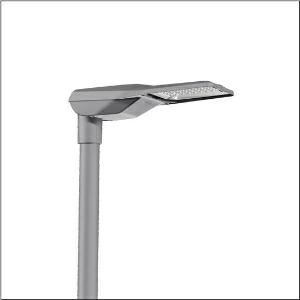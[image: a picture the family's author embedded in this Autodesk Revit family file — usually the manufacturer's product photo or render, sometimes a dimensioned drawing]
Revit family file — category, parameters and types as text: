
# Revit family: streetlight_sl_21_iq_mini___st0_8a_5xe2c41g08hb_fab9
name_source: partatom
category: Lighting Fixtures
units: mm (PartAtom-declared; Revit-internal decimal feet)

## family parameters
Cut with Voids When Loaded = No
Host = Face
Light Source = No
Part Type = Normal
Room Calculation Point = No
Round Connector Dimension = Use Diameter
Shared = No

## types (1)
- --- (1 x LED, 9860 lm, 70.9 W, 4000K)
    Apparent Load = 71 VA
    CIE Flux Codes = 38 75 97 100 100
    Color Rendering = 70
    Color Temperature = 4000K
    Default Elevation = 1800 mm
    Description = Streetlight SL 21 iQ mini, mast luminaire, primary light control with lens, of PMMA, primary optical cover: cover, of toughened safety glass, transparent, light distribution: ST0.8a, light emission: direct distribution, primary light characteristic: asymmetric, installation type: post-top, side-entry, LED, High Power LED, rated luminous flux: 9.860lm, luminous efficacy: 139lm/W, light colour: 740, colour temperature: 4000K, control: Street-Remote, Auto-Match, Temp-Guard, Lumen-Switch, Night-Set, Smart-Wire, Light-Fading, Desk-Remote (wireless, voltage-free reading and setting of iQ features in the workshop via application-optimized NFC function/RFID function), optimised constant luminous flux control (CLO 2.0), presetting dimming linear, mains connection: 220..240V, AC, 50/60Hz, start of lifetime: 71W, end of service life: 75W, reduction: 31W, luminaire housing, of diecast aluminium, powder-coated, Siteco® metallic grey (DB 702S), corrosivity category C5 mid according to DIN EN ISO 12944, please order mast flange separately, inclination adjustable: 0°, 5°, 10°, 15°, sealing non-destructively replaceable, multi-level sealing system, length: 628mm, width: 235mm, height: 110mm, mast flange for spigot size: 42mm (side-entry): 5XC10008XM4, 60/48mm (side-entry/post-top): 5XC10108XM2, 76/60mm (side-entry/post-top): 5XC10108XM1, protection rating (complete): IP66, insulation class (complete): insulation class II (safety insulation), certification: CE, ENEC, ENEC+, VDE, impact resistance: IK09, permissible operating ambient temperature for outdoor applications: -40..+50°C, standard-compliant lighting for roads and squares, packaging unit: 1 piece

Light Distribution: ST0.8a
    Height = 110 mm
    Lamp = 1 x LED
    Lamp Light Flux = 9860 lm
    Lamp Power = 70.9 W
    Lamp count = 1
    Length = 625 mm
    Luminous efficacy = 139 lm/W
    Manufacturer = Siteco
    ModVariant = No
    Model = 5XE2C41G08HB
    Number of Poles = 1
    OnlyDefault = Yes
    Power Factor = 1
    Product Name = Streetlight SL 21 iQ mini | ST0.8a
    Product group = mast luminaire | pylon top
    ProductGroupID = 6100
    Protection Class = Protection class II
    Protection Degree = IP 66
    RLX_Detail_Level = 1
    RLX_Emergency_Light_Flux = 0 lm
    RLX_Emergency_Type = 0
    RLX_Emergency_Type_DB = No
    RlxData = <blob elided: 92657 chars, md5=61518901>
    Socket = socket
    Standby Power = 0 W
    System Light Flux = 9860 lm
    System Power = 71 W
    Type Comments = factory setting: luminous flux: 100 % | dim-lin: 254 | 711 mA
    Type Image = l_1003519.jpg
    URL = http://relux.com
    VarID = @adj_107511
    Voltage = 0 V
    Weight = 0.00 kg
    Width = 234 mm

## geometry (parser evidence)
native form markers: Blend x4, Sweep x11
no freeform markers — native parametric forms only
